# Revit family: Bidet-DXV-Fitzgerald-D25000004.415
name_source: partatom
category: Plumbing Fixtures
units: mm (PartAtom-declared; Revit-internal decimal feet)

## family parameters
Always vertical = No
Cut with Voids When Loaded = No
OmniClass Number = 23.45.05.14.27
OmniClass Title = Bidets
Part Type = Normal
Room Calculation Point = No
Round Connector Dimension = Use Radius
Shared = Yes
Work Plane-Based = Yes

## types (1)
- D25000004.415
    Assembly Code = D2010910
    Bowl Length = 14 1/4"
    Bowl Width = 9 7/8"
    CW Connection = Yes
    CWFU = 1.5
    Cold Water Connection Diameter = 3/8"
    Cold Water Connection Height = 7"
    Cold Water Connection Radius = 3/16"
    Cold Water Connection Width = 3"
    Default Elevation = 0"
    Description = Fitzgerald Bidet
    Finish = Vitreous China-DXV-415-Canvas White
    HW Connection = Yes
    HWFU = 1.5
    Height = 15 1/2"
    Hot Water Connection Diameter = 0"
    Hot Water Connection Height = 7"
    Hot Water Connection Radius = 3/16"
    Hot Water Connection Width = 3"
    Installation Instruction Link = https://dxv01.blob.core.windows.net
    Installation Type = Floor Mounted
    Length = 25 9/16"
    Manufacturer = DXV
    Material = Vitreous China-DXV-415-Canvas White
    Model = D25000004.415
    Price = Prices may vary. Please consult Manufacturer Representative for most up-to-date price list.
    Product Documentation Link = https://dxv01.blob.core.windows.net
    Product Page URL = https://www.dxv.com
    Revised Date = 10/12/2021
    URL = www.dxv.com
    Vent Connection = No
    WFU = 2
    Warranty Documentation Link = https://www.dxv.com
    Waste Connection = Yes
    Waste Connection Diameter = 1 1/4"
    Waste Connection Height = 4"
    Waste Connection Radius = 5/8"
    Waste Connection Width = 1 1/8"
    Width = 15 5/16"

## geometry (parser evidence)
native form markers: Sweep x2
no freeform markers — native parametric forms only
